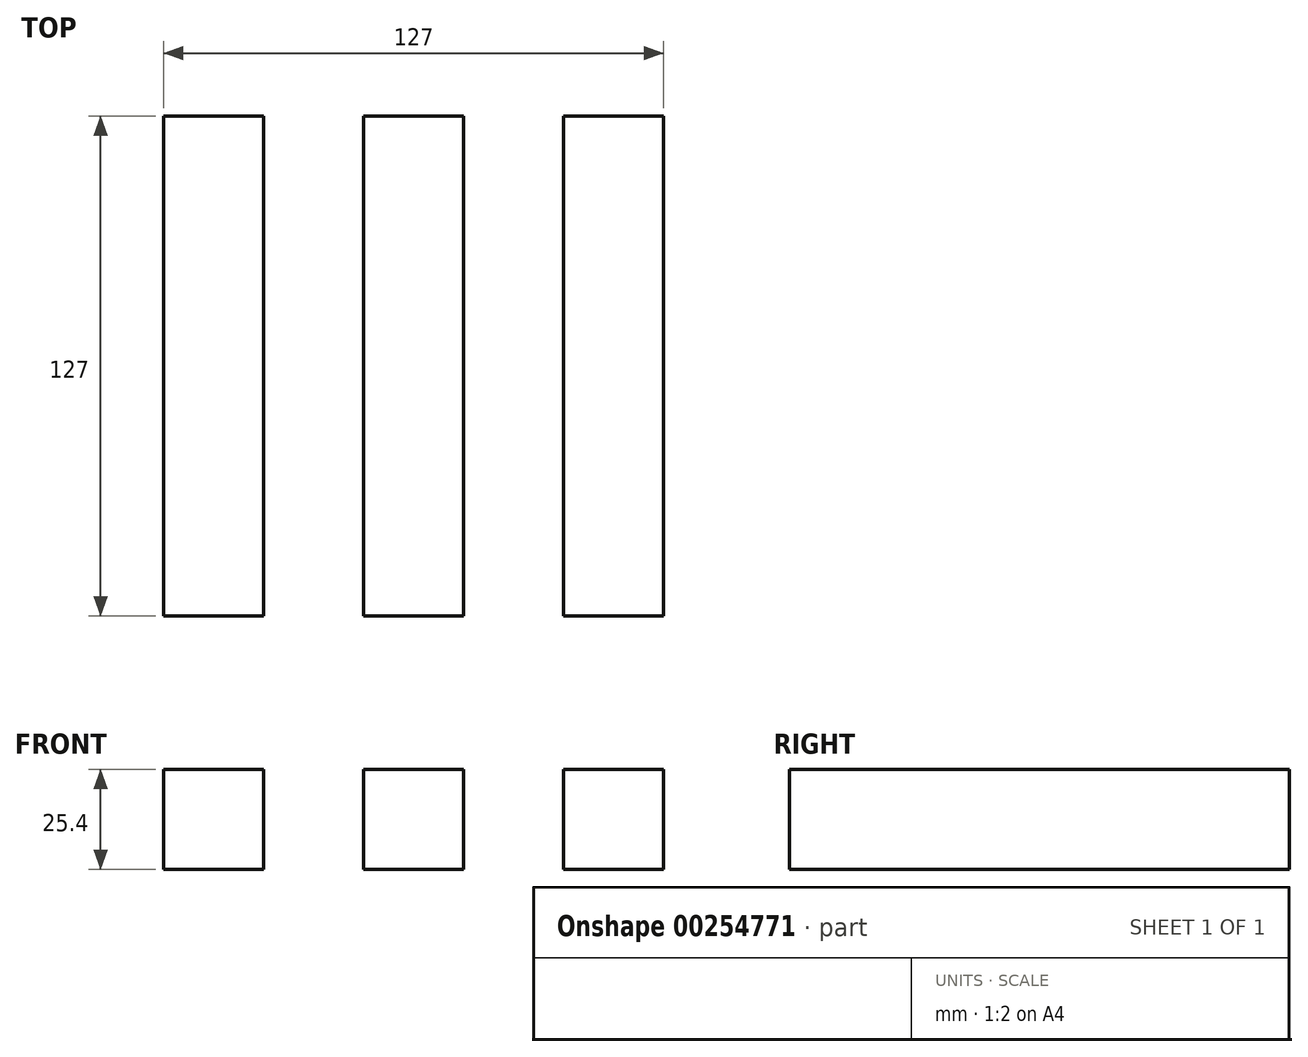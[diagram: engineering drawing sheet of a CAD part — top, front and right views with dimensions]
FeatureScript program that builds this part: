
annotation { "Feature Type Name" : "Feature", "Feature Type Description" : "" }
export const myFeature = defineFeature(function(context is Context, id is Id, definition is map)
    precondition{}
    {
        {
            var Q0;
            Q0=qCreatedBy(makeId("Front.planeOp"),FACE);
            var sketch = newSketch(context, id + "F0", { "sketchPlane" : qUnion([Q0])});
            skLineSegment(sketch, "E0.bottom", {"start": v(12.7, -12.7) * mm, "end": v(-12.7, -12.7) * mm});
            skLineSegment(sketch, "E0.top", {"start": v(12.7, 12.7) * mm, "end": v(-12.7, 12.7) * mm});
            skLineSegment(sketch, "E0.left", {"start": v(12.7, -12.7) * mm, "end": v(12.7, 12.7) * mm});
            skLineSegment(sketch, "E0.right", {"start": v(-12.7, -12.7) * mm, "end": v(-12.7, 12.7) * mm});
            skPoint(sketch, "E0.middle", {"position": v(0, 0) * mm});
            skLineSegment(sketch, "E1.bottom", {"start": v(38.1, -12.7) * mm, "end": v(63.5, -12.7) * mm});
            skLineSegment(sketch, "E1.top", {"start": v(38.1, 12.7) * mm, "end": v(63.5, 12.7) * mm});
            skLineSegment(sketch, "E1.left", {"start": v(38.1, -12.7) * mm, "end": v(38.1, 12.7) * mm});
            skLineSegment(sketch, "E1.right", {"start": v(63.5, -12.7) * mm, "end": v(63.5, 12.7) * mm});
            skPoint(sketch, "E1.middle", {"position": v(50.8, 0) * mm});
            skPoint(sketch, "E2.endSnap0", {"position": v(-12.7, 0) * mm});
            skLineSegment(sketch, "E3.bottom", {"start": v(-38.1, -12.7) * mm, "end": v(-63.5, -12.7) * mm});
            skLineSegment(sketch, "E3.top", {"start": v(-38.1, 12.7) * mm, "end": v(-63.5, 12.7) * mm});
            skLineSegment(sketch, "E3.left", {"start": v(-38.1, -12.7) * mm, "end": v(-38.1, 12.7) * mm});
            skLineSegment(sketch, "E3.right", {"start": v(-63.5, -12.7) * mm, "end": v(-63.5, 12.7) * mm});
            skPoint(sketch, "E3.middle", {"position": v(-50.8, 0) * mm});
            skSolve(sketch);
        }
        {
            var Q0;
            Q0=makeQuery(id+"F0.imprint","IMPRINT",FACE,{"disambiguationData":[TD([[makeQuery(id+"F0.imprint","IMPRINT",EDGE,{"derivedFrom":sQuery(id+"F0.wireOp",EDGE,"E3.bottom")}),-1.0]])]});
            var Q1;
            Q1=makeQuery(id+"F0.imprint","IMPRINT",FACE,{"disambiguationData":[TD([[makeQuery(id+"F0.imprint","IMPRINT",EDGE,{"derivedFrom":sQuery(id+"F0.wireOp",EDGE,"E1.bottom")}),1.0]])]});
            var Q2;
            Q2=makeQuery(id+"F0.imprint","IMPRINT",FACE,{"disambiguationData":[TD([[makeQuery(id+"F0.imprint","IMPRINT",EDGE,{"derivedFrom":sQuery(id+"F0.wireOp",EDGE,"E0.bottom")}),-1.0]])]});
            extrude(context, id + "F1", {"entities" : qUnion([Q0, Q1, Q2]), "endBound" : BoundingType.SYMMETRIC, "depth" : 127 * mm});
        }
    });
